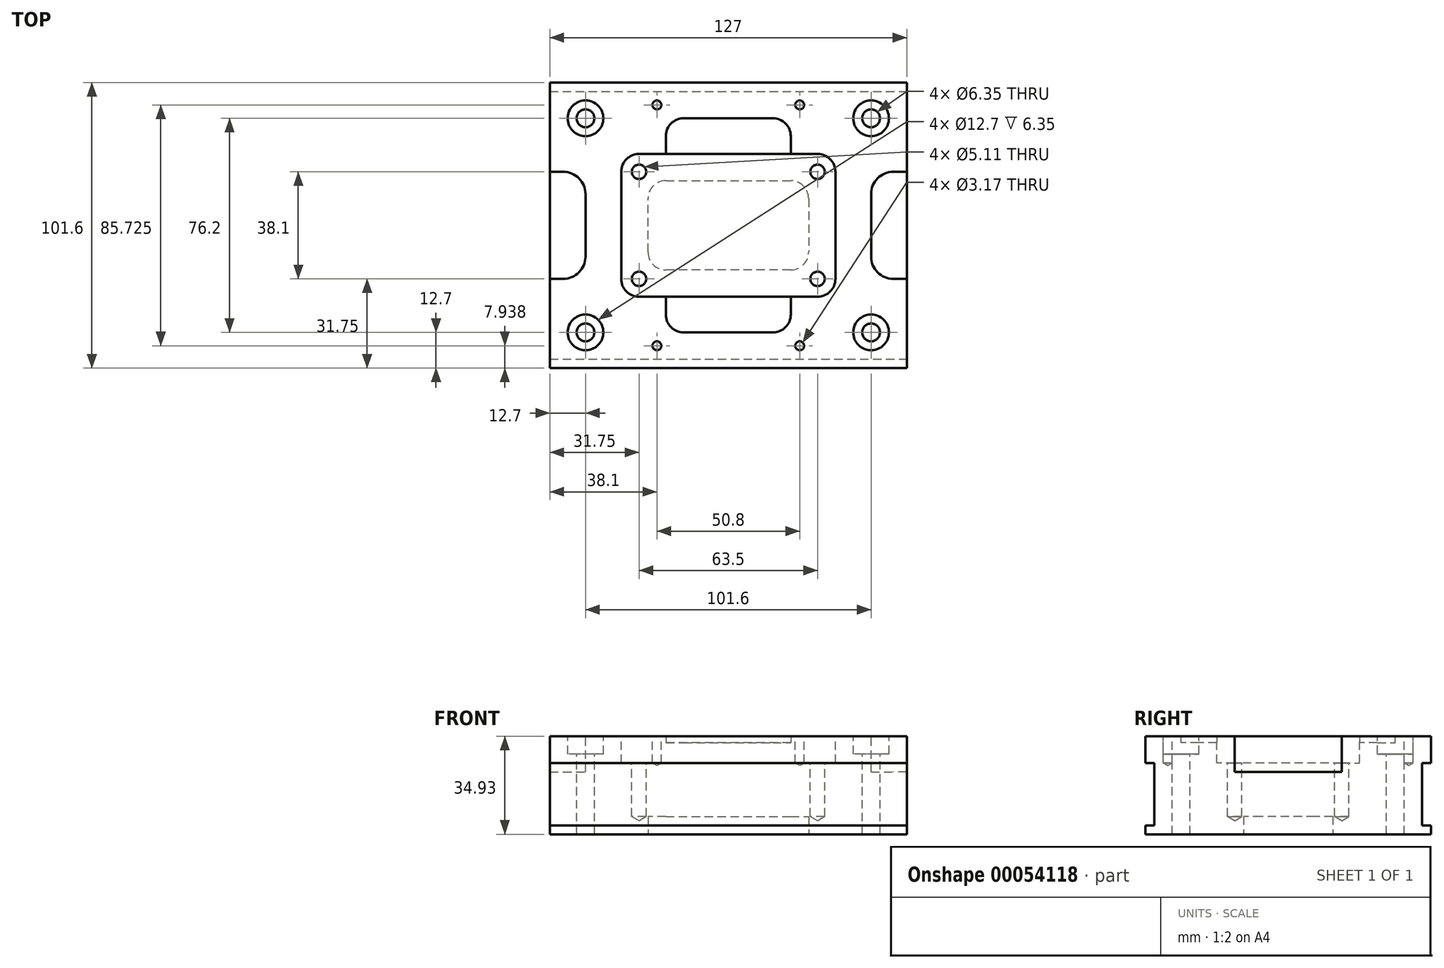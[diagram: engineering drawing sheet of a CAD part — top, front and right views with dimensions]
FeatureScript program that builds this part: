
annotation { "Feature Type Name" : "Feature", "Feature Type Description" : "" }
export const myFeature = defineFeature(function(context is Context, id is Id, definition is map)
    precondition{}
    {
        {
            var Q0;
            Q0=qCreatedBy(makeId("Top.planeOp"),FACE);
            var sketch = newSketch(context, id + "F0", { "sketchPlane" : qUnion([Q0])});
            skLineSegment(sketch, "E0.rect.bottom", {"start": v(-63.5, 50.8) * mm, "end": v(63.5, 50.8) * mm});
            skLineSegment(sketch, "E0.rect.top", {"start": v(-63.5, -50.8) * mm, "end": v(63.5, -50.8) * mm});
            skLineSegment(sketch, "E0.rect.left", {"start": v(-63.5, 50.8) * mm, "end": v(-63.5, -50.8) * mm});
            skLineSegment(sketch, "E0.rect.right", {"start": v(63.5, 50.8) * mm, "end": v(63.5, -50.8) * mm});
            skPoint(sketch, "E0.rect.middle", {"position": v(0, 0) * mm});
            skSolve(sketch);
        }
        {
            var Q0;
            Q0=makeQuery(id+"F0.imprint","IMPRINT",FACE,{"disambiguationData":[TD([[makeQuery(id+"F0.imprint","IMPRINT",EDGE,{"derivedFrom":sQuery(id+"F0.wireOp",EDGE,"E0.rect.bottom")}),-1.0]])]});
            extrude(context, id + "F1", {"entities" : qUnion([Q0]), "depth" : 38.1 * mm});
        }
        {
            var Q0;
            Q0=makeQuery(id+"F1.opExtrude","CAP_FACE",FACE,{"disambiguationData":[OSD([sQuery(id+"F0.wireOp",EDGE,"E0.rect.bottom"),sQuery(id+"F0.wireOp",EDGE,"E0.rect.top"),sQuery(id+"F0.wireOp",EDGE,"E0.rect.left"),sQuery(id+"F0.wireOp",EDGE,"E0.rect.right")])],"isStart":false});
            var sketch = newSketch(context, id + "F2", { "sketchPlane" : qUnion([Q0])});
            skLineSegment(sketch, "E1.rect.bottom", {"start": v(-38.1, 25.4) * mm, "end": v(38.1, 25.4) * mm});
            skLineSegment(sketch, "E1.rect.top", {"start": v(-38.1, -25.4) * mm, "end": v(38.1, -25.4) * mm});
            skLineSegment(sketch, "E1.rect.left", {"start": v(-38.1, 25.4) * mm, "end": v(-38.1, -25.4) * mm});
            skLineSegment(sketch, "E1.rect.right", {"start": v(38.1, 25.4) * mm, "end": v(38.1, -25.4) * mm});
            skPoint(sketch, "E1.rect.middle", {"position": v(0, 0) * mm});
            skSolve(sketch);
        }
        {
            var Q0;
            Q0=qSketchRegion(id+"F2",true);
            extrude(context, id + "F3", {"entities" : qUnion([Q0]), "operationType" : NewBodyOperationType.REMOVE, "oppositeDirection" : true, "depth" : 9.52 * mm});
        }
        {
            var Q0;
            Q0=makeQuery(id+"F3.boolean.opBoolean","COPY",EDGE,{"derivedFrom":makeQuery(id+"F3.opExtrude","SWEPT_EDGE",EDGE,{"disambiguationData":[OSD([sQuery(id+"F2.wireOp",EDGE,"E1.rect.bottom"),sQuery(id+"F2.wireOp",EDGE,"E1.rect.left")])]})});
            var Q1;
            Q1=makeQuery(id+"F3.boolean.opBoolean","COPY",EDGE,{"derivedFrom":makeQuery(id+"F3.opExtrude","SWEPT_EDGE",EDGE,{"disambiguationData":[OSD([sQuery(id+"F2.wireOp",EDGE,"E1.rect.bottom"),sQuery(id+"F2.wireOp",EDGE,"E1.rect.right")])]})});
            var Q2;
            Q2=makeQuery(id+"F3.boolean.opBoolean","COPY",EDGE,{"derivedFrom":makeQuery(id+"F3.opExtrude","SWEPT_EDGE",EDGE,{"disambiguationData":[OSD([sQuery(id+"F2.wireOp",EDGE,"E1.rect.top"),sQuery(id+"F2.wireOp",EDGE,"E1.rect.right")])]})});
            var Q3;
            Q3=makeQuery(id+"F3.boolean.opBoolean","COPY",EDGE,{"derivedFrom":makeQuery(id+"F3.opExtrude","SWEPT_EDGE",EDGE,{"disambiguationData":[OSD([sQuery(id+"F2.wireOp",EDGE,"E1.rect.top"),sQuery(id+"F2.wireOp",EDGE,"E1.rect.left")])]})});
            fillet(context, id + "F4", {"entities" : qUnion([Q0, Q1, Q2, Q3]), "radius" : 6.35 * mm, "tangentPropagation" : true, "allowEdgeOverflow" : false});
        }
        {
            var Q0;
            Q0=makeQuery(id+"F1.opExtrude","CAP_FACE",FACE,{"disambiguationData":[OSD([sQuery(id+"F0.wireOp",EDGE,"E0.rect.bottom"),sQuery(id+"F0.wireOp",EDGE,"E0.rect.top"),sQuery(id+"F0.wireOp",EDGE,"E0.rect.left"),sQuery(id+"F0.wireOp",EDGE,"E0.rect.right")])],"isStart":false});
            var sketch = newSketch(context, id + "F5", { "sketchPlane" : qUnion([Q0])});
            skPoint(sketch, "E2", {"position": v(50.8, 38.1) * mm});
            skPoint(sketch, "E3", {"position": v(50.8, -38.1) * mm});
            skPoint(sketch, "E4", {"position": v(-50.8, -38.1) * mm});
            skPoint(sketch, "E5", {"position": v(-50.8, 38.1) * mm});
            skSolve(sketch);
        }
        {
            var Q0;
            Q0=sQuery(id+"F5.wireOp",VERTEX,"E5");
            var Q1;
            Q1=sQuery(id+"F5.wireOp",VERTEX,"E2");
            var Q2;
            Q2=sQuery(id+"F5.wireOp",VERTEX,"E3");
            var Q3;
            Q3=sQuery(id+"F5.wireOp",VERTEX,"E4");
            var Q4;
            Q4=makeQuery(id+"F1.opExtrude","SWEPT_BODY",BODY,{"disambiguationData":[OSD([sQuery(id+"F0.wireOp",EDGE,"E0.rect.bottom"),sQuery(id+"F0.wireOp",EDGE,"E0.rect.top"),sQuery(id+"F0.wireOp",EDGE,"E0.rect.left"),sQuery(id+"F0.wireOp",EDGE,"E0.rect.right")])]});
            hole(context, id + "F6", {"style" : HoleStyle.C_BORE, "holeDiameter" : 6.35 * mm, "cBoreDiameter" : 12.7 * mm, "cBoreDepth" : 6.35 * mm, "endStyle" : HoleEndStyle.THROUGH, "locations" : qUnion([Q0, Q1, Q2, Q3]), "scope" : qUnion([Q4])});
        }
        {
            var Q0;
            Q0=makeQuery(id+"F1.opExtrude","SWEPT_FACE",FACE,{"disambiguationData":[OSD([sQuery(id+"F0.wireOp",EDGE,"E0.rect.right")])]});
            var sketch = newSketch(context, id + "F7", { "sketchPlane" : qUnion([Q0])});
            skLineSegment(sketch, "E6.bottom", {"start": v(-50.8, 28.57) * mm, "end": v(-47.62, 28.57) * mm});
            skLineSegment(sketch, "E6.top", {"start": v(-50.8, 6.35) * mm, "end": v(-47.62, 6.35) * mm});
            skLineSegment(sketch, "E6.left", {"start": v(-50.8, 28.57) * mm, "end": v(-50.8, 6.35) * mm});
            skLineSegment(sketch, "E6.right", {"start": v(-47.62, 28.57) * mm, "end": v(-47.62, 6.35) * mm});
            skLineSegment(sketch, "E7.bottom", {"start": v(50.8, 28.57) * mm, "end": v(47.63, 28.57) * mm});
            skLineSegment(sketch, "E7.top", {"start": v(50.8, 6.35) * mm, "end": v(47.63, 6.35) * mm});
            skLineSegment(sketch, "E7.left", {"start": v(50.8, 28.57) * mm, "end": v(50.8, 6.35) * mm});
            skLineSegment(sketch, "E7.right", {"start": v(47.63, 28.58) * mm, "end": v(47.63, 6.35) * mm});
            skSolve(sketch);
        }
        {
            var Q0;
            Q0=qSketchRegion(id+"F7",true);
            extrude(context, id + "F8", {"entities" : qUnion([Q0]), "operationType" : NewBodyOperationType.REMOVE, "endBound" : BoundingType.THROUGH_ALL, "oppositeDirection" : true, "depth" : 25.4 * mm});
        }
        {
            var Q0;
            Q0=makeQuery(id+"F3.boolean.opBoolean","COPY",FACE,{"derivedFrom":makeQuery(id+"F3.opExtrude","CAP_FACE",FACE,{"disambiguationData":[OSD([sQuery(id+"F2.wireOp",EDGE,"E1.rect.bottom"),sQuery(id+"F2.wireOp",EDGE,"E1.rect.top"),sQuery(id+"F2.wireOp",EDGE,"E1.rect.left"),sQuery(id+"F2.wireOp",EDGE,"E1.rect.right")])],"isStart":false})});
            var sketch = newSketch(context, id + "F9", { "sketchPlane" : qUnion([Q0])});
            skPoint(sketch, "E8", {"position": v(-31.75, 19.05) * mm});
            skPoint(sketch, "E9", {"position": v(-31.75, -19.05) * mm});
            skPoint(sketch, "E10", {"position": v(31.75, 19.05) * mm});
            skPoint(sketch, "E11", {"position": v(31.75, -19.05) * mm});
            skSolve(sketch);
        }
        {
            var Q0;
            Q0=sQuery(id+"F9.wireOp",VERTEX,"E8");
            var Q1;
            Q1=sQuery(id+"F9.wireOp",VERTEX,"E9");
            var Q2;
            Q2=sQuery(id+"F9.wireOp",VERTEX,"E11");
            var Q3;
            Q3=sQuery(id+"F9.wireOp",VERTEX,"E10");
            var Q4;
            Q4=makeQuery(id+"F1.opExtrude","SWEPT_BODY",BODY,{"disambiguationData":[OSD([sQuery(id+"F0.wireOp",EDGE,"E0.rect.bottom"),sQuery(id+"F0.wireOp",EDGE,"E0.rect.top"),sQuery(id+"F0.wireOp",EDGE,"E0.rect.left"),sQuery(id+"F0.wireOp",EDGE,"E0.rect.right")])]});
            hole(context, id + "F10", {"style" : HoleStyle.SIMPLE, "holeDiameter" : 5.1 * mm, "endStyle" : HoleEndStyle.BLIND, "holeDepth" : 19.05 * mm, "locations" : qUnion([Q0, Q1, Q2, Q3]), "scope" : qUnion([Q4])});
        }
        {
            var Q0;
            Q0=makeQuery(id+"F1.opExtrude","CAP_FACE",FACE,{"disambiguationData":[OSD([sQuery(id+"F0.wireOp",EDGE,"E0.rect.bottom"),sQuery(id+"F0.wireOp",EDGE,"E0.rect.top"),sQuery(id+"F0.wireOp",EDGE,"E0.rect.left"),sQuery(id+"F0.wireOp",EDGE,"E0.rect.right")])],"isStart":false});
            var sketch = newSketch(context, id + "F11", { "sketchPlane" : qUnion([Q0])});
            skLineSegment(sketch, "E12.bottom", {"start": v(-63.5, 19.05) * mm, "end": v(-50.8, 19.05) * mm});
            skLineSegment(sketch, "E12.top", {"start": v(-63.5, -19.05) * mm, "end": v(-50.8, -19.05) * mm});
            skLineSegment(sketch, "E12.left", {"start": v(-63.5, 19.05) * mm, "end": v(-63.5, -19.05) * mm});
            skLineSegment(sketch, "E12.right", {"start": v(-50.8, 19.05) * mm, "end": v(-50.8, -19.05) * mm});
            skLineSegment(sketch, "E13.bottom", {"start": v(63.5, 19.05) * mm, "end": v(50.8, 19.05) * mm});
            skLineSegment(sketch, "E13.top", {"start": v(63.5, -19.05) * mm, "end": v(50.8, -19.05) * mm});
            skLineSegment(sketch, "E13.left", {"start": v(63.5, 19.05) * mm, "end": v(63.5, -19.05) * mm});
            skLineSegment(sketch, "E13.right", {"start": v(50.8, 19.05) * mm, "end": v(50.8, -19.05) * mm});
            skSolve(sketch);
        }
        {
            var Q0;
            Q0=qSketchRegion(id+"F11",true);
            extrude(context, id + "F12", {"entities" : qUnion([Q0]), "operationType" : NewBodyOperationType.REMOVE, "oppositeDirection" : true, "depth" : 12.7 * mm});
        }
        {
            var Q0;
            Q0=makeQuery(id+"F12.boolean.opBoolean","COPY",EDGE,{"derivedFrom":makeQuery(id+"F12.opExtrude","SWEPT_EDGE",EDGE,{"disambiguationData":[OSD([sQuery(id+"F11.wireOp",EDGE,"E12.bottom"),sQuery(id+"F11.wireOp",EDGE,"E12.right")])]})});
            var Q1;
            Q1=makeQuery(id+"F12.boolean.opBoolean","COPY",EDGE,{"derivedFrom":makeQuery(id+"F12.opExtrude","SWEPT_EDGE",EDGE,{"disambiguationData":[OSD([sQuery(id+"F11.wireOp",EDGE,"E12.top"),sQuery(id+"F11.wireOp",EDGE,"E12.right")])]})});
            var Q2;
            Q2=makeQuery(id+"F12.boolean.opBoolean","COPY",EDGE,{"derivedFrom":makeQuery(id+"F12.opExtrude","SWEPT_EDGE",EDGE,{"disambiguationData":[OSD([sQuery(id+"F11.wireOp",EDGE,"E13.bottom"),sQuery(id+"F11.wireOp",EDGE,"E13.right")])]})});
            var Q3;
            Q3=makeQuery(id+"F12.boolean.opBoolean","COPY",EDGE,{"derivedFrom":makeQuery(id+"F12.opExtrude","SWEPT_EDGE",EDGE,{"disambiguationData":[OSD([sQuery(id+"F11.wireOp",EDGE,"E13.top"),sQuery(id+"F11.wireOp",EDGE,"E13.right")])]})});
            fillet(context, id + "F13", {"entities" : qUnion([Q0, Q1, Q2, Q3]), "radius" : 7.94 * mm, "tangentPropagation" : true, "allowEdgeOverflow" : false});
        }
        {
            var Q0;
            Q0=makeQuery(id+"F1.opExtrude","CAP_FACE",FACE,{"disambiguationData":[OSD([sQuery(id+"F0.wireOp",EDGE,"E0.rect.bottom"),sQuery(id+"F0.wireOp",EDGE,"E0.rect.top"),sQuery(id+"F0.wireOp",EDGE,"E0.rect.left"),sQuery(id+"F0.wireOp",EDGE,"E0.rect.right")])],"isStart":true});
            var sketch = newSketch(context, id + "F14", { "sketchPlane" : qUnion([Q0])});
            skLineSegment(sketch, "E14.0.0", {"start": v(31.75, -25.4) * mm, "end": v(-31.75, -25.4) * mm});
            skArc(sketch, "E14.0.1", {"start": v(-31.75, -25.4) * mm, "mid": v(-36.24, -23.54) * mm, "end": v(-38.1, -19.05) * mm});
            skLineSegment(sketch, "E14.0.2", {"start": v(-38.1, -19.05) * mm, "end": v(-38.1, 19.05) * mm});
            skArc(sketch, "E14.0.3", {"start": v(-38.1, 19.05) * mm, "mid": v(-36.24, 23.54) * mm, "end": v(-31.75, 25.4) * mm});
            skLineSegment(sketch, "E14.0.4", {"start": v(-31.75, 25.4) * mm, "end": v(31.75, 25.4) * mm});
            skArc(sketch, "E14.0.5", {"start": v(31.75, 25.4) * mm, "mid": v(36.24, 23.54) * mm, "end": v(38.1, 19.05) * mm});
            skLineSegment(sketch, "E14.0.6", {"start": v(38.1, 19.05) * mm, "end": v(38.1, -19.05) * mm});
            skArc(sketch, "E14.0.7", {"start": v(38.1, -19.05) * mm, "mid": v(36.24, -23.54) * mm, "end": v(31.75, -25.4) * mm});
            skSolve(sketch);
        }
        {
            var Q0;
            Q0=qSketchRegion(id+"F14",true);
            extrude(context, id + "F15", {"entities" : qUnion([Q0]), "operationType" : NewBodyOperationType.REMOVE, "oppositeDirection" : true, "depth" : 3.17 * mm});
        }
        {
            var Q0;
            Q0=makeQuery(id+"F15.boolean.opBoolean","COPY",FACE,{"derivedFrom":makeQuery(id+"F15.opExtrude","CAP_FACE",FACE,{"disambiguationData":[OSD([sQuery(id+"F14.wireOp",EDGE,"E14.0.0"),sQuery(id+"F14.wireOp",EDGE,"E14.0.1"),sQuery(id+"F14.wireOp",EDGE,"E14.0.2"),sQuery(id+"F14.wireOp",EDGE,"E14.0.3"),sQuery(id+"F14.wireOp",EDGE,"E14.0.4"),sQuery(id+"F14.wireOp",EDGE,"E14.0.5"),sQuery(id+"F14.wireOp",EDGE,"E14.0.6"),sQuery(id+"F14.wireOp",EDGE,"E14.0.7")])],"isStart":false})});
            var sketch = newSketch(context, id + "F16", { "sketchPlane" : qUnion([Q0])});
            skLineSegment(sketch, "E15.0", {"start": v(-28.57, -15.87) * mm, "end": v(28.57, -15.87) * mm});
            skLineSegment(sketch, "E15.1", {"start": v(-28.57, 15.87) * mm, "end": v(-28.57, -15.87) * mm});
            skLineSegment(sketch, "E15.2", {"start": v(28.57, 15.87) * mm, "end": v(-28.57, 15.87) * mm});
            skLineSegment(sketch, "E15.3", {"start": v(28.57, -15.87) * mm, "end": v(28.57, 15.87) * mm});
            skSolve(sketch);
        }
        {
            var Q0;
            Q0=qSketchRegion(id+"F16",true);
            extrude(context, id + "F17", {"entities" : qUnion([Q0]), "operationType" : NewBodyOperationType.REMOVE, "oppositeDirection" : true, "depth" : 6.35 * mm});
        }
        {
            var Q0;
            Q0=makeQuery(id+"F17.boolean.opBoolean","COPY",EDGE,{"derivedFrom":makeQuery(id+"F17.opExtrude","SWEPT_EDGE",EDGE,{"disambiguationData":[OSD([sQuery(id+"F16.wireOp",EDGE,"E15.1"),sQuery(id+"F16.wireOp",EDGE,"E15.2")])]})});
            var Q1;
            Q1=makeQuery(id+"F17.boolean.opBoolean","COPY",EDGE,{"derivedFrom":makeQuery(id+"F17.opExtrude","SWEPT_EDGE",EDGE,{"disambiguationData":[OSD([sQuery(id+"F16.wireOp",EDGE,"E15.0"),sQuery(id+"F16.wireOp",EDGE,"E15.1")])]})});
            var Q2;
            Q2=makeQuery(id+"F17.boolean.opBoolean","COPY",EDGE,{"derivedFrom":makeQuery(id+"F17.opExtrude","SWEPT_EDGE",EDGE,{"disambiguationData":[OSD([sQuery(id+"F16.wireOp",EDGE,"E15.2"),sQuery(id+"F16.wireOp",EDGE,"E15.3")])]})});
            var Q3;
            Q3=makeQuery(id+"F17.boolean.opBoolean","COPY",EDGE,{"derivedFrom":makeQuery(id+"F17.opExtrude","SWEPT_EDGE",EDGE,{"disambiguationData":[OSD([sQuery(id+"F16.wireOp",EDGE,"E15.0"),sQuery(id+"F16.wireOp",EDGE,"E15.3")])]})});
            fillet(context, id + "F18", {"entities" : qUnion([Q0, Q1, Q2, Q3]), "radius" : 6.35 * mm, "tangentPropagation" : true, "allowEdgeOverflow" : false});
        }
        {
            var Q0;
            Q0=makeQuery(id+"F1.opExtrude","CAP_FACE",FACE,{"disambiguationData":[OSD([sQuery(id+"F0.wireOp",EDGE,"E0.rect.bottom"),sQuery(id+"F0.wireOp",EDGE,"E0.rect.top"),sQuery(id+"F0.wireOp",EDGE,"E0.rect.left"),sQuery(id+"F0.wireOp",EDGE,"E0.rect.right")])],"isStart":false});
            var sketch = newSketch(context, id + "F19", { "sketchPlane" : qUnion([Q0])});
            skPoint(sketch, "E16", {"position": v(-25.4, 42.86) * mm});
            skPoint(sketch, "E17", {"position": v(25.4, 42.86) * mm});
            skPoint(sketch, "E18", {"position": v(-25.4, -42.86) * mm});
            skPoint(sketch, "E19", {"position": v(25.4, -42.86) * mm});
            skSolve(sketch);
        }
        {
            var Q0;
            Q0=sQuery(id+"F19.wireOp",VERTEX,"E16");
            var Q1;
            Q1=sQuery(id+"F19.wireOp",VERTEX,"E17");
            var Q2;
            Q2=sQuery(id+"F19.wireOp",VERTEX,"E18");
            var Q3;
            Q3=sQuery(id+"F19.wireOp",VERTEX,"E19");
            var Q4;
            Q4=makeQuery(id+"F1.opExtrude","SWEPT_BODY",BODY,{"disambiguationData":[OSD([sQuery(id+"F0.wireOp",EDGE,"E0.rect.bottom"),sQuery(id+"F0.wireOp",EDGE,"E0.rect.top"),sQuery(id+"F0.wireOp",EDGE,"E0.rect.left"),sQuery(id+"F0.wireOp",EDGE,"E0.rect.right")])]});
            hole(context, id + "F20", {"style" : HoleStyle.SIMPLE, "holeDiameter" : 3.17 * mm, "endStyle" : HoleEndStyle.BLIND, "holeDepth" : 9.52 * mm, "locations" : qUnion([Q0, Q1, Q2, Q3]), "scope" : qUnion([Q4])});
        }
        {
            var Q0;
            Q0=makeQuery(id+"F1.opExtrude","CAP_FACE",FACE,{"disambiguationData":[OSD([sQuery(id+"F0.wireOp",EDGE,"E0.rect.bottom"),sQuery(id+"F0.wireOp",EDGE,"E0.rect.top"),sQuery(id+"F0.wireOp",EDGE,"E0.rect.left"),sQuery(id+"F0.wireOp",EDGE,"E0.rect.right")])],"isStart":false});
            var sketch = newSketch(context, id + "F21", { "sketchPlane" : qUnion([Q0])});
            skLineSegment(sketch, "E20.bottom", {"start": v(-22.22, 38.1) * mm, "end": v(22.22, 38.1) * mm});
            skLineSegment(sketch, "E20.top", {"start": v(-22.22, -38.1) * mm, "end": v(22.22, -38.1) * mm});
            skLineSegment(sketch, "E20.left", {"start": v(-22.22, 38.1) * mm, "end": v(-22.22, -38.1) * mm});
            skLineSegment(sketch, "E20.right", {"start": v(22.22, 38.1) * mm, "end": v(22.22, -38.1) * mm});
            skSolve(sketch);
        }
        {
            var Q0;
            Q0=qSketchRegion(id+"F21",true);
            extrude(context, id + "F22", {"entities" : qUnion([Q0]), "operationType" : NewBodyOperationType.REMOVE, "oppositeDirection" : true, "depth" : 2.38 * mm});
        }
        {
            var Q0;
            Q0=makeQuery(id+"F22.boolean.opBoolean","COPY",EDGE,{"derivedFrom":makeQuery(id+"F22.opExtrude","SWEPT_EDGE",EDGE,{"disambiguationData":[OSD([sQuery(id+"F21.wireOp",EDGE,"E20.bottom"),sQuery(id+"F21.wireOp",EDGE,"E20.left")])]})});
            var Q1;
            Q1=makeQuery(id+"F22.boolean.opBoolean","COPY",EDGE,{"derivedFrom":makeQuery(id+"F22.opExtrude","SWEPT_EDGE",EDGE,{"disambiguationData":[OSD([sQuery(id+"F21.wireOp",EDGE,"E20.bottom"),sQuery(id+"F21.wireOp",EDGE,"E20.right")])]})});
            var Q2;
            Q2=makeQuery(id+"F22.boolean.opBoolean","COPY",EDGE,{"derivedFrom":makeQuery(id+"F22.opExtrude","SWEPT_EDGE",EDGE,{"disambiguationData":[OSD([sQuery(id+"F21.wireOp",EDGE,"E20.top"),sQuery(id+"F21.wireOp",EDGE,"E20.right")])]})});
            var Q3;
            Q3=makeQuery(id+"F22.boolean.opBoolean","COPY",EDGE,{"derivedFrom":makeQuery(id+"F22.opExtrude","SWEPT_EDGE",EDGE,{"disambiguationData":[OSD([sQuery(id+"F21.wireOp",EDGE,"E20.top"),sQuery(id+"F21.wireOp",EDGE,"E20.left")])]})});
            fillet(context, id + "F23", {"entities" : qUnion([Q0, Q1, Q2, Q3]), "radius" : 6.35 * mm, "tangentPropagation" : true, "allowEdgeOverflow" : false});
        }
        {
            var Q0;
            Q0=makeQuery(id+"F1.opExtrude","CAP_FACE",FACE,{"disambiguationData":[OSD([sQuery(id+"F0.wireOp",EDGE,"E0.rect.bottom"),sQuery(id+"F0.wireOp",EDGE,"E0.rect.top"),sQuery(id+"F0.wireOp",EDGE,"E0.rect.left"),sQuery(id+"F0.wireOp",EDGE,"E0.rect.right")])],"isStart":true});
            var sketch = newSketch(context, id + "F24", { "sketchPlane" : qUnion([Q0])});
            skLineSegment(sketch, "E21.rect.bottom", {"start": v(-101.6, 76.2) * mm, "end": v(101.6, 76.2) * mm});
            skLineSegment(sketch, "E21.rect.top", {"start": v(-101.6, -76.2) * mm, "end": v(101.6, -76.2) * mm});
            skLineSegment(sketch, "E21.rect.left", {"start": v(-101.6, 76.2) * mm, "end": v(-101.6, -76.2) * mm});
            skLineSegment(sketch, "E21.rect.right", {"start": v(101.6, 76.2) * mm, "end": v(101.6, -76.2) * mm});
            skPoint(sketch, "E21.rect.middle", {"position": v(0, 0) * mm});
            skSolve(sketch);
        }
        {
            var Q0;
            Q0=qSketchRegion(id+"F24",true);
            extrude(context, id + "F25", {"entities" : qUnion([Q0]), "depth" : 25.4 * mm, "hasSecondDirection" : true, "secondDirectionOppositeDirection" : true, "secondDirectionDepth" : 3.17 * mm});
        }
        {
            var Q0;
            Q0=makeQuery(id+"F25.opExtrude","CAP_FACE",FACE,{"disambiguationData":[OSD([sQuery(id+"F24.wireOp",EDGE,"E21.rect.bottom"),sQuery(id+"F24.wireOp",EDGE,"E21.rect.top"),sQuery(id+"F24.wireOp",EDGE,"E21.rect.left"),sQuery(id+"F24.wireOp",EDGE,"E21.rect.right")])],"isStart":true});
            var sketch = newSketch(context, id + "F26", { "sketchPlane" : qUnion([Q0])});
            skLineSegment(sketch, "E22.bottom", {"start": v(-63.5, 50.8) * mm, "end": v(63.5, 50.8) * mm});
            skLineSegment(sketch, "E22.top", {"start": v(-63.5, -50.8) * mm, "end": v(63.5, -50.8) * mm});
            skLineSegment(sketch, "E22.left", {"start": v(-63.5, 50.8) * mm, "end": v(-63.5, -50.8) * mm});
            skLineSegment(sketch, "E22.right", {"start": v(63.5, 50.8) * mm, "end": v(63.5, -50.8) * mm});
            skSolve(sketch);
        }
        {
            var Q0;
            Q0=qSketchRegion(id+"F26",true);
            extrude(context, id + "F27", {"entities" : qUnion([Q0]), "operationType" : NewBodyOperationType.REMOVE, "oppositeDirection" : true, "depth" : 3.17 * mm});
        }
        {
            var Q0;
            Q0=makeQuery(id+"F25.opExtrude","CAP_FACE",FACE,{"disambiguationData":[OSD([sQuery(id+"F24.wireOp",EDGE,"E21.rect.bottom"),sQuery(id+"F24.wireOp",EDGE,"E21.rect.top"),sQuery(id+"F24.wireOp",EDGE,"E21.rect.left"),sQuery(id+"F24.wireOp",EDGE,"E21.rect.right")])],"isStart":true});
            var sketch = newSketch(context, id + "F28", { "sketchPlane" : qUnion([Q0])});
            skCircle(sketch, "E23", {"center": v(-63.5, 50.8) * mm, "radius": 4.76 * mm});
            skCircle(sketch, "E24", {"center": v(-63.5, -50.8) * mm, "radius": 4.76 * mm});
            skCircle(sketch, "E25", {"center": v(63.5, 50.8) * mm, "radius": 4.76 * mm});
            skCircle(sketch, "E26", {"center": v(63.5, -50.8) * mm, "radius": 4.76 * mm});
            skSolve(sketch);
        }
        {
            var Q0;
            Q0=qSketchRegion(id+"F28",true);
            extrude(context, id + "F29", {"entities" : qUnion([Q0]), "operationType" : NewBodyOperationType.REMOVE, "endBound" : BoundingType.THROUGH_ALL, "oppositeDirection" : true, "depth" : 25.4 * mm});
        }
        {
            var Q0;
            Q0=makeQuery(id+"F25.opExtrude","SWEPT_BODY",BODY,{"disambiguationData":[OSD([sQuery(id+"F24.wireOp",EDGE,"E21.rect.bottom"),sQuery(id+"F24.wireOp",EDGE,"E21.rect.top"),sQuery(id+"F24.wireOp",EDGE,"E21.rect.left"),sQuery(id+"F24.wireOp",EDGE,"E21.rect.right")])]});
            deleteBodies(context, id + "F30", {"entities" : qUnion([Q0])});
        }
    });
